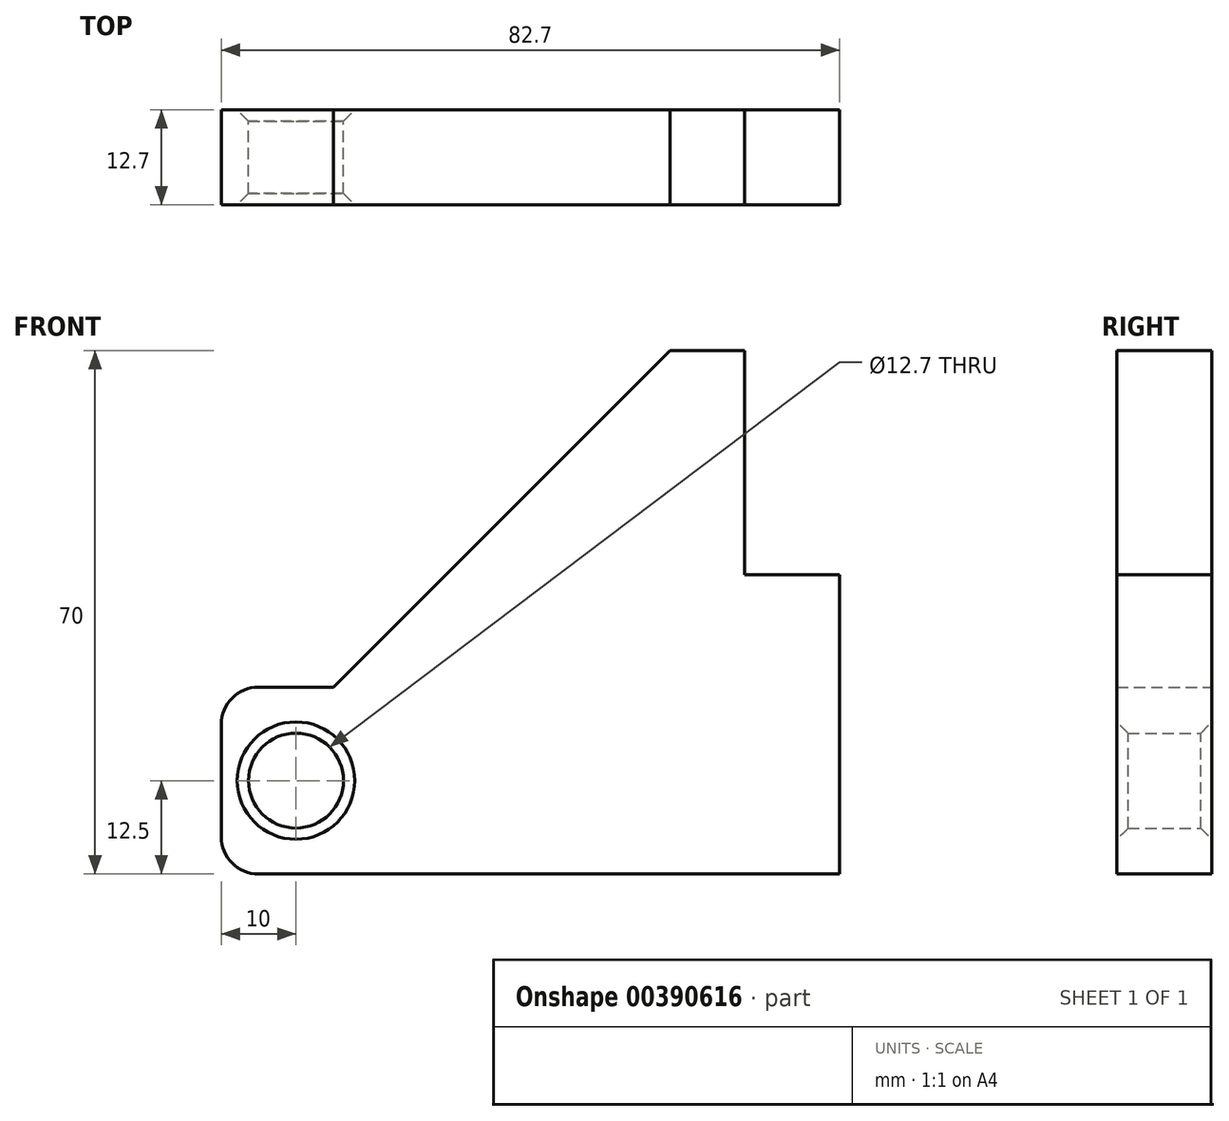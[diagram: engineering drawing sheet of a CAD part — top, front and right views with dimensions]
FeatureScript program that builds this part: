
annotation { "Feature Type Name" : "Feature", "Feature Type Description" : "" }
export const myFeature = defineFeature(function(context is Context, id is Id, definition is map)
    precondition{}
    {
        {
            var Q0;
            Q0=qCreatedBy(makeId("Front.planeOp"),FACE);
            var sketch = newSketch(context, id + "F0", { "sketchPlane" : qUnion([Q0])});
            skLineSegment(sketch, "E0", {"start": v(-70, 5) * mm, "end": v(-70, 20) * mm});
            skLineSegment(sketch, "E1", {"start": v(-65, 25) * mm, "end": v(-55, 25) * mm});
            skLineSegment(sketch, "E2", {"start": v(-55, 25) * mm, "end": v(-10, 70) * mm});
            skLineSegment(sketch, "E3", {"start": v(-10, 70) * mm, "end": v(0, 70) * mm});
            skLineSegment(sketch, "E4", {"start": v(0, 70) * mm, "end": v(0, 40) * mm});
            skLineSegment(sketch, "E5", {"start": v(0, 40) * mm, "end": v(12.7, 40) * mm});
            skLineSegment(sketch, "E6", {"start": v(12.7, 40) * mm, "end": v(12.7, 0) * mm});
            skLineSegment(sketch, "E7", {"start": v(12.7, 0) * mm, "end": v(-65, 0) * mm});
            skLineSegment(sketch, "E8", {"start": v(-70, 12.5) * mm, "end": v(12.7, 12.5) * mm, "construction": true});
            skCircle(sketch, "E9", {"center": v(-60, 12.5) * mm, "radius": 6.35 * mm});
            skLineSegment(sketch, "E10", {"start": v(0, 40) * mm, "end": v(0, 0) * mm, "construction": true});
            skPoint(sketch, "E11.visualSharp", {"position": v(-70, 25) * mm});
            skArc(sketch, "E11.filletArc", {"start": v(-65, 25) * mm, "mid": v(-68.54, 23.54) * mm, "end": v(-70, 20) * mm});
            skPoint(sketch, "E12.visualSharp", {"position": v(-70, 0) * mm});
            skArc(sketch, "E12.filletArc", {"start": v(-70, 5) * mm, "mid": v(-68.54, 1.46) * mm, "end": v(-65, 0) * mm});
            skSolve(sketch);
        }
        {
            var Q0;
            Q0 = qSketchRegion(id + "F0", true);
            extrude(context, id + "F1", {"entities" : qUnion([Q0]), "depth" : 12.7 * mm});
        }
        {
            var Q0;
            Q0=makeQuery(id+"F1.opExtrude","CAP_EDGE",EDGE,{"disambiguationData":[OSD([sQuery(id+"F0.wireOp",EDGE,"E9")])],"isStart":true});
            var Q1;
            Q1=makeQuery(id+"F1.opExtrude","CAP_EDGE",EDGE,{"disambiguationData":[OSD([sQuery(id+"F0.wireOp",EDGE,"E9")])],"isStart":false});
            chamfer(context, id + "F2", {"entities" : qUnion([Q0, Q1]), "width" : 1.5 * mm, "tangentPropagation" : true});
        }
    });
